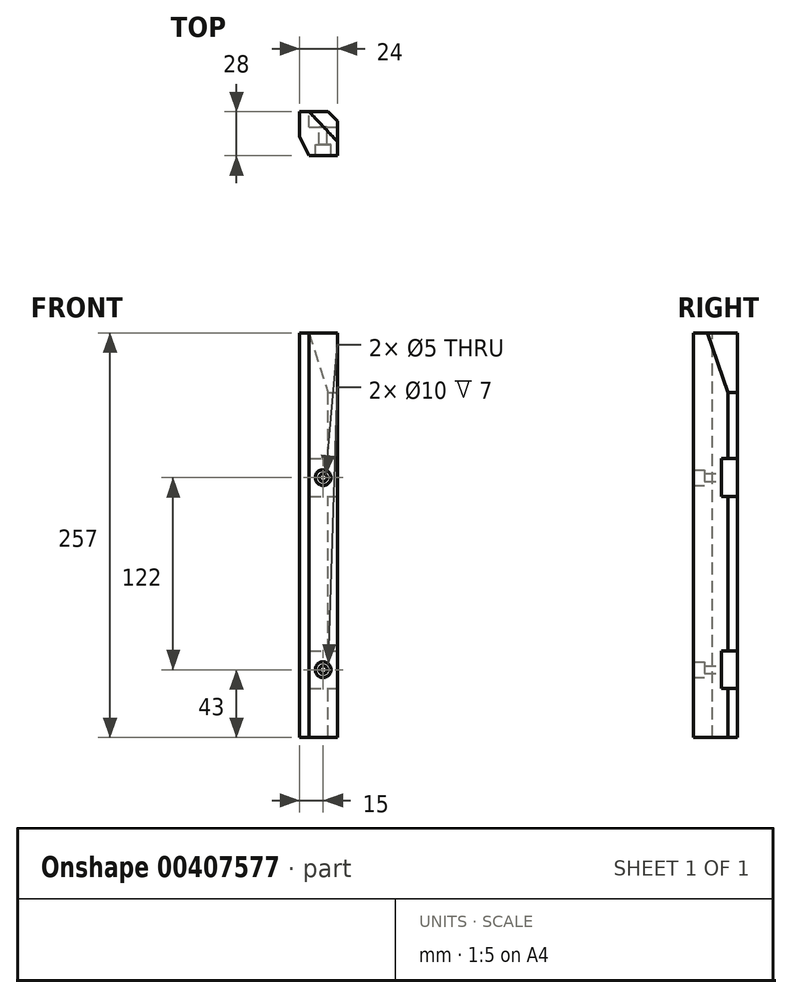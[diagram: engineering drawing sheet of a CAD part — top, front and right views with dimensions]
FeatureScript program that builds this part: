
annotation { "Feature Type Name" : "Feature", "Feature Type Description" : "" }
export const myFeature = defineFeature(function(context is Context, id is Id, definition is map)
    precondition{}
    {
        {
            var Q0;
            Q0=qCreatedBy(makeId("Top.planeOp"),FACE);
            var sketch = newSketch(context, id + "F0", { "sketchPlane" : qUnion([Q0])});
            skLineSegment(sketch, "E0", {"start": v(-6, 0) * mm, "end": v(0, -6) * mm});
            skLineSegment(sketch, "E1", {"start": v(0, -6) * mm, "end": v(0, -28) * mm});
            skLineSegment(sketch, "E2", {"start": v(0, -28) * mm, "end": v(-18, -28) * mm});
            skLineSegment(sketch, "E3", {"start": v(-18, -28) * mm, "end": v(-24, -16) * mm});
            skLineSegment(sketch, "E4", {"start": v(-24, -16) * mm, "end": v(-24, 0) * mm});
            skLineSegment(sketch, "E5", {"start": v(-24, 0) * mm, "end": v(-6, 0) * mm});
            skSolve(sketch);
        }
        {
            var Q0;
            Q0=makeQuery(id+"F0.imprint","IMPRINT",FACE,{"disambiguationData":[TD([[makeQuery(id+"F0.imprint","IMPRINT",EDGE,{"derivedFrom":sQuery(id+"F0.wireOp",EDGE,"E0")}),-1.0]])]});
            extrude(context, id + "F1", {"entities" : qUnion([Q0]), "oppositeDirection" : true, "depth" : 257 * mm});
        }
        {
            var Q0;
            Q0=makeQuery(id+"F1.opExtrude","SWEPT_FACE",FACE,{"disambiguationData":[OSD([sQuery(id+"F0.wireOp",EDGE,"E1")])]});
            var sketch = newSketch(context, id + "F2", { "sketchPlane" : qUnion([Q0])});
            skLineSegment(sketch, "E6.bottom", {"start": v(-10, -226) * mm, "end": v(0, -226) * mm});
            skLineSegment(sketch, "E6.top", {"start": v(-10, -202) * mm, "end": v(0, -202) * mm});
            skLineSegment(sketch, "E6.left", {"start": v(-10, -226) * mm, "end": v(-10, -202) * mm});
            skLineSegment(sketch, "E6.right", {"start": v(0, -226) * mm, "end": v(0, -202) * mm});
            skLineSegment(sketch, "E7.bottom", {"start": v(-10, -104) * mm, "end": v(0, -104) * mm});
            skLineSegment(sketch, "E7.top", {"start": v(-10, -80) * mm, "end": v(0, -80) * mm});
            skLineSegment(sketch, "E7.left", {"start": v(-10, -104) * mm, "end": v(-10, -80) * mm});
            skLineSegment(sketch, "E7.right", {"start": v(0, -104) * mm, "end": v(0, -80) * mm});
            skSolve(sketch);
        }
        {
            var Q0;
            {var subQ0=sQuery(id+"F2.wireOp",EDGE,"E6.left");Q0=makeQuery(id+"F2.imprint","IMPRINT",FACE,{"disambiguationData":[TD([[makeQuery(id+"F2.imprint","IMPRINT",EDGE,{"derivedFrom":subQ0}),-1.0]])]});}
            var Q1;
            {var subQ0=sQuery(id+"F2.wireOp",EDGE,"E6.right");Q1=makeQuery(id+"F2.imprint","IMPRINT",FACE,{"disambiguationData":[TD([[makeQuery(id+"F2.imprint","IMPRINT",EDGE,{"derivedFrom":subQ0}),1.0]])]});}
            var Q2;
            {var subQ0=sQuery(id+"F2.wireOp",EDGE,"E7.left");Q2=makeQuery(id+"F2.imprint","IMPRINT",FACE,{"disambiguationData":[TD([[makeQuery(id+"F2.imprint","IMPRINT",EDGE,{"derivedFrom":subQ0}),-1.0]])]});}
            var Q3;
            {var subQ0=sQuery(id+"F2.wireOp",EDGE,"E7.right");Q3=makeQuery(id+"F2.imprint","IMPRINT",FACE,{"disambiguationData":[TD([[makeQuery(id+"F2.imprint","IMPRINT",EDGE,{"derivedFrom":subQ0}),1.0]])]});}
            extrude(context, id + "F3", {"entities" : qUnion([Q0, Q1, Q2, Q3]), "operationType" : NewBodyOperationType.REMOVE, "oppositeDirection" : true, "depth" : 18 * mm});
        }
        {
            var Q0;
            Q0=makeQuery(id+"F3.boolean.opBoolean","COPY",FACE,{"derivedFrom":makeQuery(id+"F3.opExtrude","SWEPT_FACE",FACE,{"disambiguationData":[OSD([sQuery(id+"F2.wireOp",EDGE,"E6.left")])]})});
            var sketch = newSketch(context, id + "F4", { "sketchPlane" : qUnion([Q0])});
            skCircle(sketch, "E8", {"center": v(9, -214) * mm, "radius": 2.5 * mm});
            skPoint(sketch, "E8.centerSnap0", {"position": v(18, -214) * mm});
            skPoint(sketch, "E8.centerSnap1", {"position": v(9, -226) * mm});
            skCircle(sketch, "E9", {"center": v(9, -214) * mm, "radius": 5 * mm});
            skCircle(sketch, "E10", {"center": v(9, -92) * mm, "radius": 2.5 * mm});
            skCircle(sketch, "E11", {"center": v(9, -92) * mm, "radius": 5 * mm});
            skSolve(sketch);
        }
        {
            var Q0;
            Q0=makeQuery(id+"F4.imprint","IMPRINT",FACE,{"disambiguationData":[TD([[makeQuery(id+"F4.imprint","IMPRINT",EDGE,{"derivedFrom":sQuery(id+"F4.wireOp",EDGE,"E10")}),1.0]])]});
            var Q1;
            Q1=makeQuery(id+"F4.imprint","IMPRINT",FACE,{"disambiguationData":[TD([[makeQuery(id+"F4.imprint","IMPRINT",EDGE,{"derivedFrom":sQuery(id+"F4.wireOp",EDGE,"E8")}),1.0]])]});
            var Q2;
            Q2=sQuery(id+"F4.wireOp",EDGE,"E8");
            var Q3;
            Q3=sQuery(id+"F4.wireOp",EDGE,"E10");
            extrude(context, id + "F5", {"entities" : qUnion([Q0, Q1]), "operationType" : NewBodyOperationType.REMOVE, "surfaceEntities" : qUnion([Q2, Q3]), "oppositeDirection" : true, "depth" : 11 * mm});
        }
        {
            var Q0;
            Q0=makeQuery(id+"F4.imprint","IMPRINT",FACE,{"disambiguationData":[TD([[makeQuery(id+"F4.imprint","IMPRINT",EDGE,{"derivedFrom":sQuery(id+"F4.wireOp",EDGE,"E8")}),-1.0]])]});
            var Q1;
            Q1=makeQuery(id+"F4.imprint","IMPRINT",FACE,{"disambiguationData":[TD([[makeQuery(id+"F4.imprint","IMPRINT",EDGE,{"derivedFrom":sQuery(id+"F4.wireOp",EDGE,"E10")}),-1.0]])]});
            var Q2;
            Q2=makeQuery(id+"F4.imprint","IMPRINT",FACE,{"disambiguationData":[TD([[makeQuery(id+"F4.imprint","IMPRINT",EDGE,{"derivedFrom":sQuery(id+"F4.wireOp",EDGE,"E8")}),1.0]])]});
            var Q3;
            Q3=makeQuery(id+"F4.imprint","IMPRINT",FACE,{"disambiguationData":[TD([[makeQuery(id+"F4.imprint","IMPRINT",EDGE,{"derivedFrom":sQuery(id+"F4.wireOp",EDGE,"E10")}),1.0]])]});
            extrude(context, id + "F6", {"entities" : qUnion([Q0, Q1, Q2, Q3]), "operationType" : NewBodyOperationType.REMOVE, "oppositeDirection" : true, "depth" : 18 * mm, "hasSecondDirection" : true, "secondDirectionOppositeDirection" : true, "secondDirectionDepth" : 11 * mm});
        }
        {
            var Q0;
            Q0=qCreatedBy(makeId("Top.planeOp"),FACE);
            cPlane(context, id + "F7", {"entities" : qUnion([Q0]), "cplaneType" : CPlaneType.OFFSET, "offset" : .1 * mm, "width" : 150 * mm, "height" : 150 * mm});
        }
        {
            var Q0;
            Q0=qCreatedBy(id+"F7.planeOp",FACE);
            var sketch = newSketch(context, id + "F8", { "sketchPlane" : qUnion([Q0])});
            skLineSegment(sketch, "E12", {"start": v(-18, 0) * mm, "end": v(0, -19) * mm});
            skLineSegment(sketch, "E13", {"start": v(0, -19) * mm, "end": v(0, 0) * mm});
            skLineSegment(sketch, "E14", {"start": v(0, 0) * mm, "end": v(-18, 0) * mm});
            skSolve(sketch);
        }
        {
            var Q0;
            Q0=qCreatedBy(makeId("Top.planeOp"),FACE);
            cPlane(context, id + "F9", {"entities" : qUnion([Q0]), "cplaneType" : CPlaneType.OFFSET, "offset" : 38 * mm, "oppositeDirection" : true, "width" : 150 * mm, "height" : 150 * mm});
        }
        {
            var Q0;
            Q0=qCreatedBy(id+"F9.planeOp",FACE);
            var sketch = newSketch(context, id + "F10", { "sketchPlane" : qUnion([Q0])});
            skLineSegment(sketch, "E15", {"start": v(-6, 0) * mm, "end": v(0, -6) * mm});
            skLineSegment(sketch, "E16", {"start": v(0, -6) * mm, "end": v(0, 0) * mm});
            skLineSegment(sketch, "E17", {"start": v(0, 0) * mm, "end": v(-6, 0) * mm});
            skSolve(sketch);
        }
        {
            var Q1;
            Q1=makeQuery(id+"F8.imprint","IMPRINT",FACE,{"disambiguationData":[TD([[makeQuery(id+"F8.imprint","IMPRINT",EDGE,{"derivedFrom":sQuery(id+"F8.wireOp",EDGE,"E12")}),1.0]])]});
            var Q2;
            Q2=makeQuery(id+"F10.imprint","IMPRINT",FACE,{"disambiguationData":[TD([[makeQuery(id+"F10.imprint","IMPRINT",EDGE,{"derivedFrom":sQuery(id+"F10.wireOp",EDGE,"E15")}),1.0]])]});
            loft(context, id + "F11", {"operationType" : NewBodyOperationType.REMOVE, "sheetProfilesArray" : [{ "sheetProfileEntities" : qUnion([Q1]) }, { "sheetProfileEntities" : qUnion([Q2]) }]});
        }
    });
